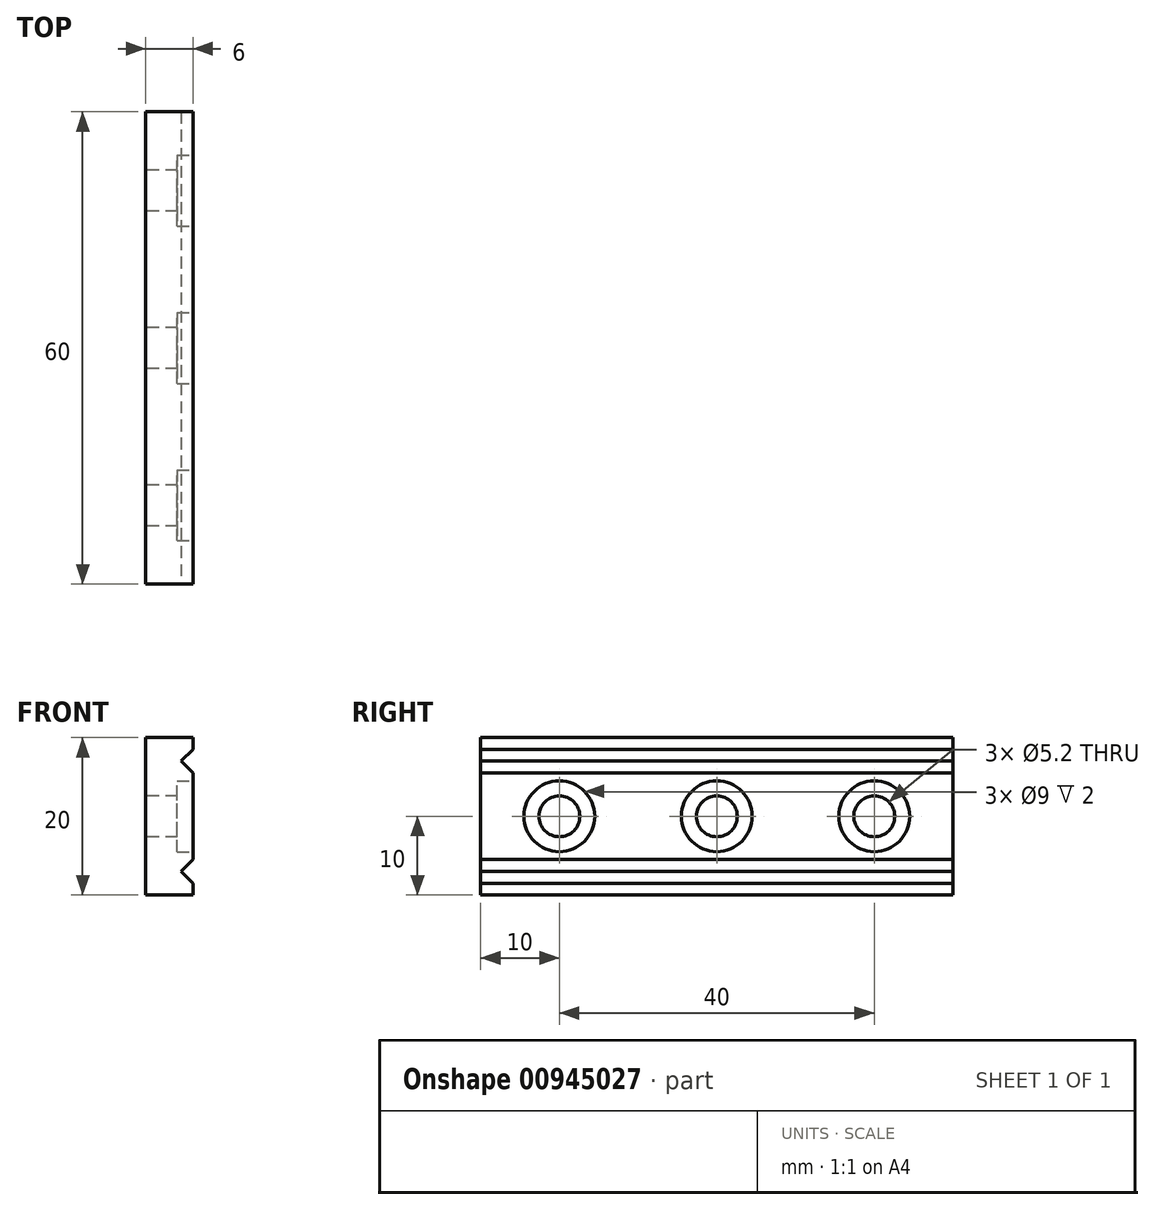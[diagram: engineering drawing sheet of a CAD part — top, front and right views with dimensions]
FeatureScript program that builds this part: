
annotation { "Feature Type Name" : "Feature", "Feature Type Description" : "" }
export const myFeature = defineFeature(function(context is Context, id is Id, definition is map)
    precondition{}
    {
        {
            var Q0;
            Q0=qCreatedBy(makeId("Right.planeOp"),FACE);
            var sketch = newSketch(context, id + "F0", { "sketchPlane" : qUnion([Q0])});
            skLineSegment(sketch, "E0.bottom", {"start": v(30, -10) * mm, "end": v(-30, -10) * mm});
            skLineSegment(sketch, "E0.top", {"start": v(30, 10) * mm, "end": v(-30, 10) * mm});
            skLineSegment(sketch, "E0.left", {"start": v(30, -10) * mm, "end": v(30, 10) * mm});
            skLineSegment(sketch, "E0.right", {"start": v(-30, -10) * mm, "end": v(-30, 10) * mm});
            skPoint(sketch, "E0.middle", {"position": v(0, 0) * mm});
            skCircle(sketch, "E1", {"center": v(-20, 0) * mm, "radius": 2.6 * mm});
            skCircle(sketch, "E2", {"center": v(20, 0) * mm, "radius": 2.6 * mm});
            skCircle(sketch, "E3", {"center": v(0, 0) * mm, "radius": 2.6 * mm});
            skSolve(sketch);
        }
        {
            var Q0;
            Q0=makeQuery(id+"F0.imprint","IMPRINT",FACE,{"disambiguationData":[TD([[makeQuery(id+"F0.imprint","IMPRINT",EDGE,{"derivedFrom":sQuery(id+"F0.wireOp",EDGE,"E0.bottom")}),-1.0]])]});
            extrude(context, id + "F1", {"entities" : qUnion([Q0]), "depth" : 6 * mm});
        }
        {
            var Q0;
            Q0=makeQuery(id+"F1.opExtrude","CAP_FACE",FACE,{"disambiguationData":[OSD([sQuery(id+"F0.wireOp",EDGE,"E0.bottom"),sQuery(id+"F0.wireOp",EDGE,"E0.top"),sQuery(id+"F0.wireOp",EDGE,"E0.left"),sQuery(id+"F0.wireOp",EDGE,"E0.right"),sQuery(id+"F0.wireOp",EDGE,"E1"),sQuery(id+"F0.wireOp",EDGE,"E2"),sQuery(id+"F0.wireOp",EDGE,"E3")])],"isStart":false});
            var sketch = newSketch(context, id + "F2", { "sketchPlane" : qUnion([Q0])});
            skCircle(sketch, "E4", {"center": v(-20, 0) * mm, "radius": 4.5 * mm});
            skCircle(sketch, "E5", {"center": v(0, 0) * mm, "radius": 4.5 * mm});
            skCircle(sketch, "E6", {"center": v(20, 0) * mm, "radius": 4.5 * mm});
            skSolve(sketch);
        }
        {
            var Q0;
            Q0=qSketchRegion(id+"F2",true);
            extrude(context, id + "F3", {"entities" : qUnion([Q0]), "operationType" : NewBodyOperationType.REMOVE, "oppositeDirection" : true, "depth" : 2 * mm});
        }
        {
            var Q0;
            Q0=makeQuery(id+"F1.opExtrude","SWEPT_FACE",FACE,{"disambiguationData":[OSD([sQuery(id+"F0.wireOp",EDGE,"E0.right")])]});
            var sketch = newSketch(context, id + "F4", { "sketchPlane" : qUnion([Q0])});
            skLineSegment(sketch, "E7", {"start": v(4.5, 7) * mm, "end": v(6.79, 9.29) * mm});
            skLineSegment(sketch, "E8", {"start": v(4.5, 7) * mm, "end": v(7.4, 4.1) * mm});
            skLineSegment(sketch, "E9", {"start": v(4.5, -7) * mm, "end": v(7.13, -4.37) * mm});
            skLineSegment(sketch, "E10", {"start": v(4.5, -7) * mm, "end": v(10.17, -12.67) * mm});
            skSolve(sketch);
        }
        {
            var Q0;
            {var subQ0=sQuery(id+"F4.wireOp",EDGE,"E8");var subQ1=sQuery(id+"F4.wireOp",EDGE,"E7");var subQ2=makeQuery(id+"F4.imprint","INTERSECT",VERTEX,{"derivedFrom":[subQ1,subQ0]});Q0=makeQuery(id+"F4.imprint","IMPRINT",FACE,{"disambiguationData":[TD([[makeQuery(id+"F4.imprint","IMPRINT",EDGE,{"disambiguationData":[TD([[subQ2,-1.0]])],"derivedFrom":subQ1}),-1.0]])]});}
            var Q1;
            {var subQ0=sQuery(id+"F4.wireOp",EDGE,"E10");var subQ1=sQuery(id+"F4.wireOp",EDGE,"E9");var subQ2=makeQuery(id+"F4.imprint","INTERSECT",VERTEX,{"derivedFrom":[subQ1,subQ0]});Q1=makeQuery(id+"F4.imprint","IMPRINT",FACE,{"disambiguationData":[TD([[makeQuery(id+"F4.imprint","IMPRINT",EDGE,{"disambiguationData":[TD([[subQ2,-1.0]])],"derivedFrom":subQ1}),-1.0]])]});}
            extrude(context, id + "F5", {"entities" : qUnion([Q0, Q1]), "operationType" : NewBodyOperationType.REMOVE, "endBound" : BoundingType.THROUGH_ALL, "oppositeDirection" : true, "depth" : 25 * mm});
        }
    });
